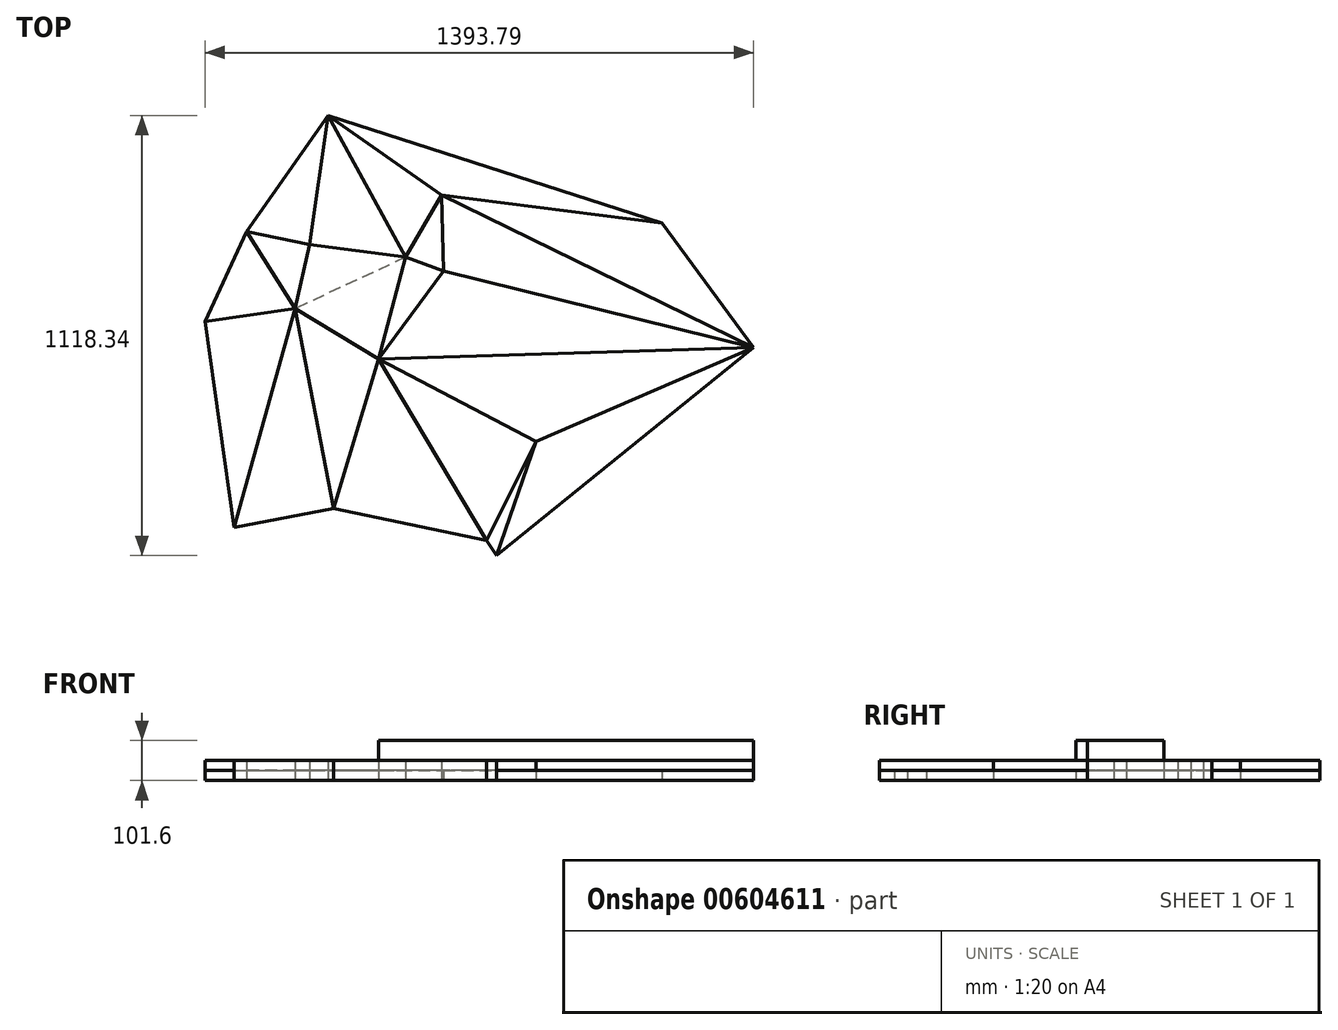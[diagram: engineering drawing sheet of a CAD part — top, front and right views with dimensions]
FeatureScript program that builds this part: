
annotation { "Feature Type Name" : "Feature", "Feature Type Description" : "" }
export const myFeature = defineFeature(function(context is Context, id is Id, definition is map)
    precondition{}
    {
        {
            var Q0;
            Q0=qCreatedBy(makeId("Top.planeOp"),FACE);
            var sketch = newSketch(context, id + "F0", { "sketchPlane" : qUnion([Q0])});
            skLineSegment(sketch, "E0", {"start": v(296.5, 12.99) * mm, "end": v(190.82, -215.19) * mm});
            skLineSegment(sketch, "E1", {"start": v(190.82, -215.19) * mm, "end": v(419.87, -182.71) * mm});
            skLineSegment(sketch, "E2", {"start": v(419.87, -182.71) * mm, "end": v(296.5, 12.99) * mm});
            skLineSegment(sketch, "E3", {"start": v(456.85, -19.49) * mm, "end": v(419.87, -182.71) * mm});
            skLineSegment(sketch, "E4", {"start": v(631.55, -310.89) * mm, "end": v(700.96, -52.43) * mm});
            skLineSegment(sketch, "E5", {"start": v(700.96, -52.43) * mm, "end": v(419.87, -182.71) * mm});
            skLineSegment(sketch, "E6", {"start": v(631.55, -310.89) * mm, "end": v(419.87, -182.71) * mm});
            skLineSegment(sketch, "E7", {"start": v(456.85, -19.49) * mm, "end": v(700.96, -52.43) * mm});
            skLineSegment(sketch, "E8", {"start": v(296.5, 12.99) * mm, "end": v(456.85, -19.49) * mm});
            skLineSegment(sketch, "E9", {"start": v(503.06, 308.08) * mm, "end": v(700.96, -52.43) * mm});
            skLineSegment(sketch, "E10", {"start": v(503.06, 308.08) * mm, "end": v(456.85, -19.49) * mm});
            skLineSegment(sketch, "E11", {"start": v(503.06, 308.08) * mm, "end": v(296.5, 12.99) * mm});
            skLineSegment(sketch, "E12", {"start": v(791.64, 106) * mm, "end": v(700.96, -52.43) * mm});
            skLineSegment(sketch, "E13", {"start": v(503.06, 308.08) * mm, "end": v(791.64, 106) * mm});
            skLineSegment(sketch, "E14", {"start": v(796.66, -87.76) * mm, "end": v(791.64, 106) * mm});
            skLineSegment(sketch, "E15", {"start": v(796.66, -87.76) * mm, "end": v(700.96, -52.43) * mm});
            skLineSegment(sketch, "E16", {"start": v(796.66, -87.76) * mm, "end": v(631.55, -310.89) * mm});
            skLineSegment(sketch, "E17", {"start": v(1584.6, -282.34) * mm, "end": v(791.64, 106) * mm});
            skLineSegment(sketch, "E18", {"start": v(796.66, -87.76) * mm, "end": v(1584.6, -282.34) * mm});
            skLineSegment(sketch, "E19", {"start": v(631.55, -310.89) * mm, "end": v(1584.6, -282.34) * mm});
            skLineSegment(sketch, "E20", {"start": v(1351.91, 34.65) * mm, "end": v(1584.6, -282.34) * mm});
            skLineSegment(sketch, "E21", {"start": v(1351.91, 34.65) * mm, "end": v(791.64, 106) * mm});
            skLineSegment(sketch, "E22", {"start": v(1351.91, 34.65) * mm, "end": v(503.06, 308.08) * mm});
            skLineSegment(sketch, "E23", {"start": v(190.82, -215.19) * mm, "end": v(265.1, -739.15) * mm});
            skLineSegment(sketch, "E24", {"start": v(265.1, -739.15) * mm, "end": v(419.87, -182.71) * mm});
            skLineSegment(sketch, "E25", {"start": v(517.55, -690.52) * mm, "end": v(631.55, -310.89) * mm});
            skLineSegment(sketch, "E26", {"start": v(517.55, -690.52) * mm, "end": v(517.55, -690.52) * mm});
            skLineSegment(sketch, "E27", {"start": v(419.87, -182.71) * mm, "end": v(517.55, -690.52) * mm});
            skLineSegment(sketch, "E28", {"start": v(265.1, -739.15) * mm, "end": v(517.55, -690.52) * mm});
            skLineSegment(sketch, "E29", {"start": v(905.88, -772.37) * mm, "end": v(631.55, -310.89) * mm});
            skLineSegment(sketch, "E30", {"start": v(905.88, -772.37) * mm, "end": v(517.55, -690.52) * mm});
            skLineSegment(sketch, "E31", {"start": v(932.06, -810.26) * mm, "end": v(1584.6, -282.34) * mm});
            skLineSegment(sketch, "E32", {"start": v(1031.6, -520.3) * mm, "end": v(932.06, -810.26) * mm});
            skLineSegment(sketch, "E33", {"start": v(1031.6, -520.3) * mm, "end": v(905.88, -772.37) * mm});
            skLineSegment(sketch, "E34", {"start": v(1031.6, -520.3) * mm, "end": v(631.55, -310.89) * mm});
            skLineSegment(sketch, "E35", {"start": v(1031.6, -520.3) * mm, "end": v(1584.6, -282.34) * mm});
            skLineSegment(sketch, "E36", {"start": v(932.06, -810.26) * mm, "end": v(905.88, -772.37) * mm});
            skSolve(sketch);
        }
        {
            var Q0;
            Q0=makeQuery(id+"F0.imprint","IMPRINT",FACE,{"disambiguationData":[TD([[makeQuery(id+"F0.imprint","IMPRINT",EDGE,{"derivedFrom":sQuery(id+"F0.wireOp",EDGE,"E31")}),1.0]])]});
            var Q1;
            Q1=makeQuery(id+"F0.imprint","IMPRINT",FACE,{"disambiguationData":[TD([[makeQuery(id+"F0.imprint","IMPRINT",EDGE,{"derivedFrom":sQuery(id+"F0.wireOp",EDGE,"E29")}),-1.0]])]});
            var Q2;
            Q2=makeQuery(id+"F0.imprint","IMPRINT",FACE,{"disambiguationData":[TD([[makeQuery(id+"F0.imprint","IMPRINT",EDGE,{"derivedFrom":sQuery(id+"F0.wireOp",EDGE,"E6")}),1.0]])]});
            var Q3;
            Q3=makeQuery(id+"F0.imprint","IMPRINT",FACE,{"disambiguationData":[TD([[makeQuery(id+"F0.imprint","IMPRINT",EDGE,{"derivedFrom":sQuery(id+"F0.wireOp",EDGE,"E1")}),-1.0]])]});
            var Q4;
            Q4=makeQuery(id+"F0.imprint","IMPRINT",FACE,{"disambiguationData":[TD([[makeQuery(id+"F0.imprint","IMPRINT",EDGE,{"derivedFrom":sQuery(id+"F0.wireOp",EDGE,"E2")}),-1.0]])]});
            var Q5;
            Q5=makeQuery(id+"F0.imprint","IMPRINT",FACE,{"disambiguationData":[TD([[makeQuery(id+"F0.imprint","IMPRINT",EDGE,{"derivedFrom":sQuery(id+"F0.wireOp",EDGE,"E4")}),-1.0]])]});
            var Q6;
            Q6=makeQuery(id+"F0.imprint","IMPRINT",FACE,{"disambiguationData":[TD([[makeQuery(id+"F0.imprint","IMPRINT",EDGE,{"derivedFrom":sQuery(id+"F0.wireOp",EDGE,"E14")}),-1.0]])]});
            var Q7;
            Q7=makeQuery(id+"F0.imprint","IMPRINT",FACE,{"disambiguationData":[TD([[makeQuery(id+"F0.imprint","IMPRINT",EDGE,{"derivedFrom":sQuery(id+"F0.wireOp",EDGE,"E13")}),1.0]])]});
            var Q8;
            Q8=makeQuery(id+"F0.imprint","IMPRINT",FACE,{"disambiguationData":[TD([[makeQuery(id+"F0.imprint","IMPRINT",EDGE,{"derivedFrom":sQuery(id+"F0.wireOp",EDGE,"E7")}),1.0]])]});
            extrude(context, id + "F1", {"entities" : qUnion([Q0, Q1, Q2, Q3, Q4, Q5, Q6, Q7, Q8]), "depth" : 25.4 * mm, "offsetDistance" : 25.4 * mm});
        }
        {
            var Q0;
            Q0=makeQuery(id+"F0.imprint","IMPRINT",FACE,{"disambiguationData":[TD([[makeQuery(id+"F0.imprint","IMPRINT",EDGE,{"derivedFrom":sQuery(id+"F0.wireOp",EDGE,"E8")}),1.0]])]});
            var Q1;
            Q1=makeQuery(id+"F0.imprint","IMPRINT",FACE,{"disambiguationData":[TD([[makeQuery(id+"F0.imprint","IMPRINT",EDGE,{"derivedFrom":sQuery(id+"F0.wireOp",EDGE,"E0")}),1.0]])]});
            var Q2;
            Q2=makeQuery(id+"F0.imprint","IMPRINT",FACE,{"disambiguationData":[TD([[makeQuery(id+"F0.imprint","IMPRINT",EDGE,{"derivedFrom":sQuery(id+"F0.wireOp",EDGE,"E3")}),1.0]])]});
            var Q3;
            Q3=makeQuery(id+"F0.imprint","IMPRINT",FACE,{"disambiguationData":[TD([[makeQuery(id+"F0.imprint","IMPRINT",EDGE,{"derivedFrom":sQuery(id+"F0.wireOp",EDGE,"E9")}),1.0]])]});
            var Q4;
            Q4=makeQuery(id+"F0.imprint","IMPRINT",FACE,{"disambiguationData":[TD([[makeQuery(id+"F0.imprint","IMPRINT",EDGE,{"derivedFrom":sQuery(id+"F0.wireOp",EDGE,"E17")}),-1.0]])]});
            var Q5;
            Q5=makeQuery(id+"F0.imprint","IMPRINT",FACE,{"disambiguationData":[TD([[makeQuery(id+"F0.imprint","IMPRINT",EDGE,{"derivedFrom":sQuery(id+"F0.wireOp",EDGE,"E19")}),-1.0]])]});
            var Q6;
            Q6=makeQuery(id+"F0.imprint","IMPRINT",FACE,{"disambiguationData":[TD([[makeQuery(id+"F0.imprint","IMPRINT",EDGE,{"derivedFrom":sQuery(id+"F0.wireOp",EDGE,"E32")}),-1.0]])]});
            var Q7;
            Q7=makeQuery(id+"F0.imprint","IMPRINT",FACE,{"disambiguationData":[TD([[makeQuery(id+"F0.imprint","IMPRINT",EDGE,{"derivedFrom":sQuery(id+"F0.wireOp",EDGE,"E24")}),-1.0]])]});
            var Q8;
            Q8=makeQuery(id+"F0.imprint","IMPRINT",FACE,{"disambiguationData":[TD([[makeQuery(id+"F0.imprint","IMPRINT",EDGE,{"derivedFrom":sQuery(id+"F0.wireOp",EDGE,"E25")}),-1.0]])]});
            var Q9;
            Q9=makeQuery(id+"F0.imprint","IMPRINT",FACE,{"disambiguationData":[TD([[makeQuery(id+"F0.imprint","IMPRINT",EDGE,{"derivedFrom":sQuery(id+"F0.wireOp",EDGE,"E4")}),1.0]])]});
            extrude(context, id + "F2", {"entities" : qUnion([Q0, Q1, Q2, Q3, Q4, Q5, Q6, Q7, Q8, Q9]), "depth" : 50.8 * mm, "offsetDistance" : 25.4 * mm});
        }
        {
            var Q0;
            Q0=makeQuery(id+"F0.imprint","IMPRINT",FACE,{"disambiguationData":[TD([[makeQuery(id+"F0.imprint","IMPRINT",EDGE,{"derivedFrom":sQuery(id+"F0.wireOp",EDGE,"E12")}),1.0]])]});
            var Q1;
            Q1=makeQuery(id+"F0.imprint","IMPRINT",FACE,{"disambiguationData":[TD([[makeQuery(id+"F0.imprint","IMPRINT",EDGE,{"derivedFrom":sQuery(id+"F0.wireOp",EDGE,"E4")}),1.0]])]});
            extrude(context, id + "F3", {"entities" : qUnion([Q0, Q1]), "depth" : 25.4 * mm, "offsetDistance" : 25.4 * mm});
        }
        {
            var Q0;
            Q0=makeQuery(id+"F0.imprint","IMPRINT",FACE,{"disambiguationData":[TD([[makeQuery(id+"F0.imprint","IMPRINT",EDGE,{"derivedFrom":sQuery(id+"F0.wireOp",EDGE,"E16")}),1.0]])]});
            extrude(context, id + "F4", {"entities" : qUnion([Q0]), "depth" : 101.6 * mm, "offsetDistance" : 25.4 * mm});
        }
    });
